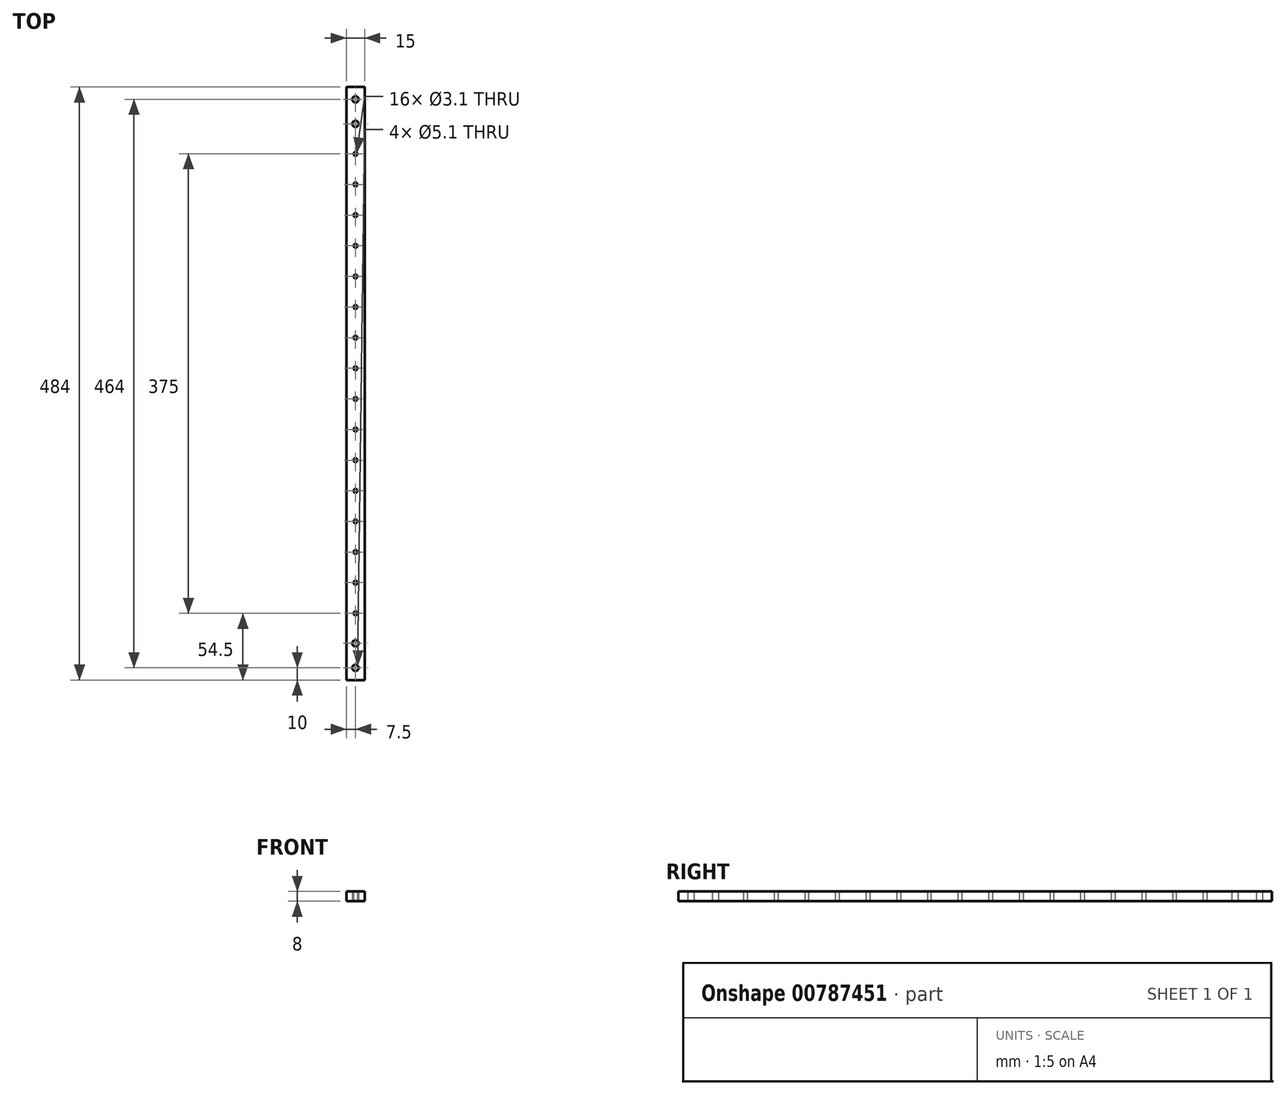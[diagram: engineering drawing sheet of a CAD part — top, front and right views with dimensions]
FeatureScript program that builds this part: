
annotation { "Feature Type Name" : "Feature", "Feature Type Description" : "" }
export const myFeature = defineFeature(function(context is Context, id is Id, definition is map)
    precondition{}
    {
        {
            var Q0;
            Q0=qCreatedBy(makeId("Top.planeOp"),FACE);
            var sketch = newSketch(context, id + "F0", { "sketchPlane" : qUnion([Q0])});
            skLineSegment(sketch, "E0.bottom", {"start": v(7.5, -242) * mm, "end": v(-7.5, -242) * mm});
            skLineSegment(sketch, "E0.top", {"start": v(7.5, 242) * mm, "end": v(-7.5, 242) * mm});
            skLineSegment(sketch, "E0.left", {"start": v(7.5, -242) * mm, "end": v(7.5, 242) * mm});
            skLineSegment(sketch, "E0.right", {"start": v(-7.5, -242) * mm, "end": v(-7.5, 242) * mm});
            skPoint(sketch, "E0.middle", {"position": v(0, 0) * mm});
            skLineSegment(sketch, "E1", {"start": v(0, -242) * mm, "end": v(0, 242) * mm, "construction": true});
            skLineSegment(sketch, "E2", {"start": v(-80.46, 187.5) * mm, "end": v(92.95, 187.5) * mm, "construction": true});
            skCircle(sketch, "E3", {"center": v(0, 187.5) * mm, "radius": 1.55 * mm});
            skCircle(sketch, "E4.1.0.0", {"center": v(0, 162.5) * mm, "radius": 1.55 * mm});
            skCircle(sketch, "E4.2.0.0", {"center": v(0, 137.5) * mm, "radius": 1.55 * mm});
            skCircle(sketch, "E4.3.0.0", {"center": v(0, 112.5) * mm, "radius": 1.55 * mm});
            skCircle(sketch, "E4.4.0.0", {"center": v(0, 87.5) * mm, "radius": 1.55 * mm});
            skCircle(sketch, "E4.5.0.0", {"center": v(0, 62.5) * mm, "radius": 1.55 * mm});
            skCircle(sketch, "E4.6.0.0", {"center": v(0, 37.5) * mm, "radius": 1.55 * mm});
            skCircle(sketch, "E4.7.0.0", {"center": v(0, 12.5) * mm, "radius": 1.55 * mm});
            skCircle(sketch, "E4.8.0.0", {"center": v(0, -12.5) * mm, "radius": 1.55 * mm});
            skCircle(sketch, "E4.9.0.0", {"center": v(0, -37.5) * mm, "radius": 1.55 * mm});
            skCircle(sketch, "E4.10.0.0", {"center": v(0, -62.5) * mm, "radius": 1.55 * mm});
            skCircle(sketch, "E4.11.0.0", {"center": v(0, -87.5) * mm, "radius": 1.55 * mm});
            skCircle(sketch, "E4.12.0.0", {"center": v(0, -112.5) * mm, "radius": 1.55 * mm});
            skCircle(sketch, "E4.13.0.0", {"center": v(0, -137.5) * mm, "radius": 1.55 * mm});
            skCircle(sketch, "E4.14.0.0", {"center": v(0, -162.5) * mm, "radius": 1.55 * mm});
            skCircle(sketch, "E4.15.0.0", {"center": v(0, -187.5) * mm, "radius": 1.55 * mm});
            skLineSegment(sketch, "E4.direction1", {"start": v(0, 187.5) * mm, "end": v(0, 162.5) * mm, "construction": true});
            skCircle(sketch, "E5", {"center": v(0, 232) * mm, "radius": 2.55 * mm});
            skCircle(sketch, "E6", {"center": v(0, 212) * mm, "radius": 2.55 * mm});
            skCircle(sketch, "E7.MirrorC", {"center": v(0, -232) * mm, "radius": 2.55 * mm});
            skCircle(sketch, "E8.MirrorC", {"center": v(0, -212) * mm, "radius": 2.55 * mm});
            skSolve(sketch);
        }
        {
            var Q0;
            Q0=makeQuery(id+"F0.imprint","IMPRINT",FACE,{"disambiguationData":[TD([[makeQuery(id+"F0.imprint","IMPRINT",EDGE,{"derivedFrom":sQuery(id+"F0.wireOp",EDGE,"E0.bottom")}),-1.0]])]});
            extrude(context, id + "F1", {"entities" : qUnion([Q0]), "depth" : 8 * mm, "offsetDistance" : 25 * mm});
        }
    });
